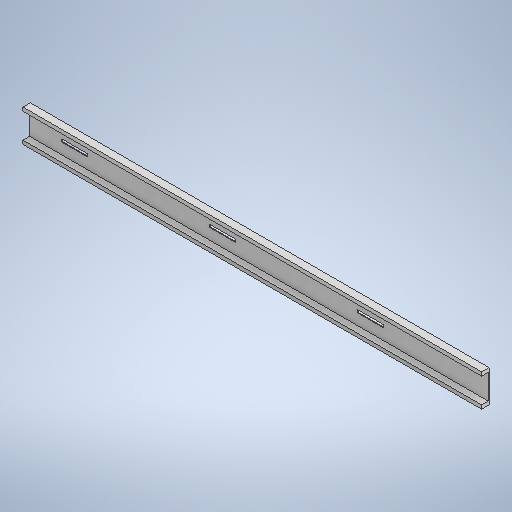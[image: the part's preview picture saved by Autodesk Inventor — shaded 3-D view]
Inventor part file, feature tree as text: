
AUTODESK INVENTOR PART (.ipt)
format: ipt  version: 2025.1 (Build 291241020, 241B)  size: 295,936 bytes
history: native  units: in
note: dims shown in document units (in); Inventor stores cm internally (conversion verified against a paired STEP export)
features: sketch x2, extrude x2
ambient origin geometry x8: Origin, YZ Plane, XZ Plane, XY Plane, X Axis, Y Axis, Z Axis, Center Point
bodies: Solid1 (feature_tree)
feature tree (4):
  sketch  "Sketch1"  dims[d0=6.2in d1=0.4375in]
  extrude  "Extrusion1"  Depth=0.4375in
  extrude  "Extrusion2"  Depth=0.05in
  sketch  "Sketch Rectangular Pattern1"  dims[d2=0.05in d3=0.05in d4=0.15in d5=0.15in d6=0.3518in d7=1.1811in d9=2.0in d10=0.3937in d12=1.0in d14=0.1in d15=0.0in d16=0.01in d17=0.0in]
